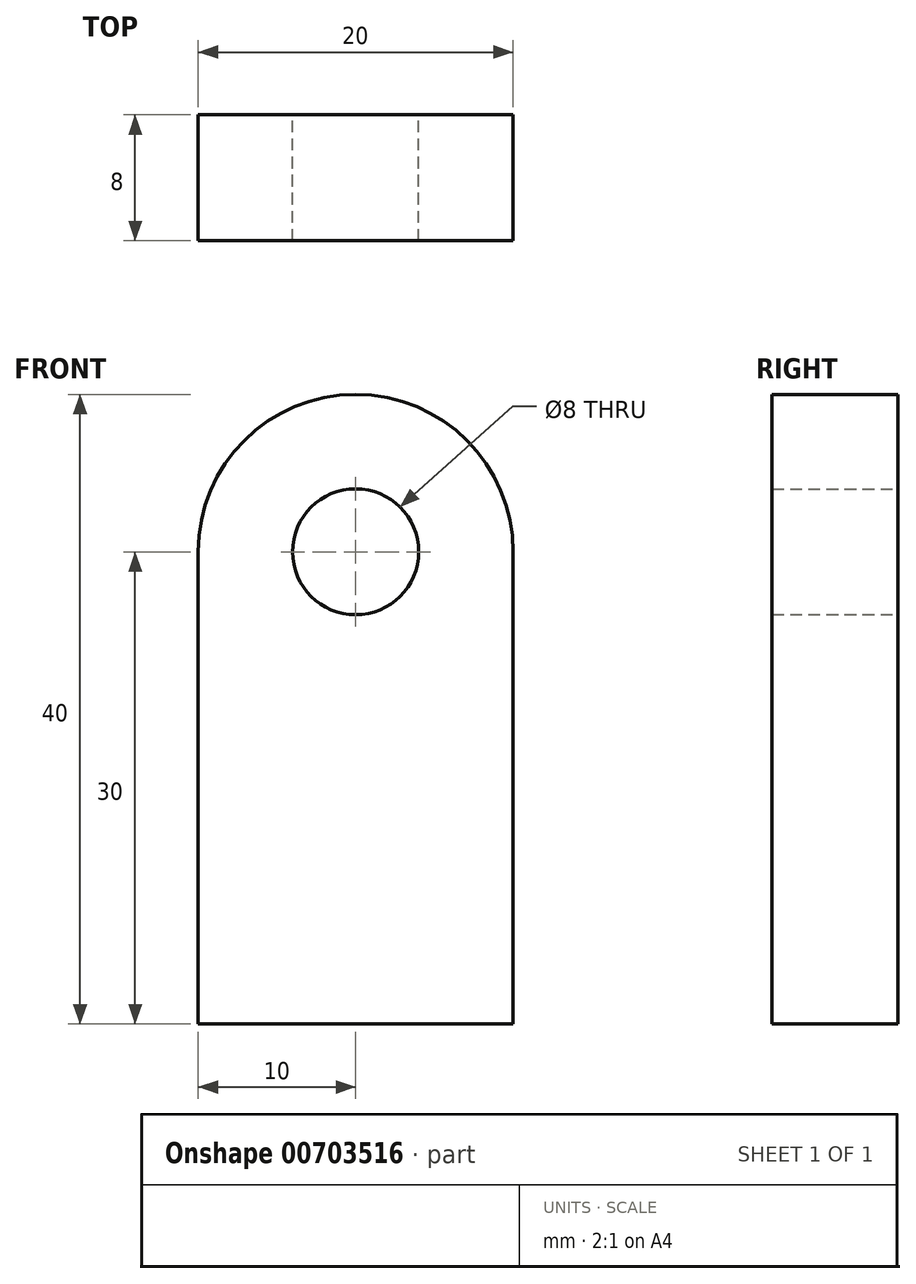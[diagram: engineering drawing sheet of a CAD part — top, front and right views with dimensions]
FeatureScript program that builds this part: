
annotation { "Feature Type Name" : "Feature", "Feature Type Description" : "" }
export const myFeature = defineFeature(function(context is Context, id is Id, definition is map)
    precondition{}
    {
        {
            var Q0;
            Q0=qCreatedBy(makeId("Front.planeOp"),FACE);
            var sketch = newSketch(context, id + "F0", { "sketchPlane" : qUnion([Q0])});
            skLineSegment(sketch, "E0.bottom", {"start": v(-10, 0) * mm, "end": v(10, 0) * mm});
            skLineSegment(sketch, "E0.left", {"start": v(-10, 0) * mm, "end": v(-10, 30) * mm});
            skLineSegment(sketch, "E0.right", {"start": v(10, 0) * mm, "end": v(10, 30) * mm});
            skArc(sketch, "E1", {"start": v(-10, 30) * mm, "mid": v(0, 40) * mm, "end": v(10, 30) * mm});
            skCircle(sketch, "E2", {"center": v(0, 30) * mm, "radius": 4 * mm});
            skSolve(sketch);
        }
        {
            var Q0;
            Q0=makeQuery(id+"F0.imprint","IMPRINT",FACE,{"disambiguationData":[TD([[makeQuery(id+"F0.imprint","IMPRINT",EDGE,{"derivedFrom":sQuery(id+"F0.wireOp",EDGE,"E0.bottom")}),1.0]])]});
            extrude(context, id + "F1", {"entities" : qUnion([Q0]), "depth" : 8 * mm, "offsetDistance" : 25.4 * mm});
        }
    });
